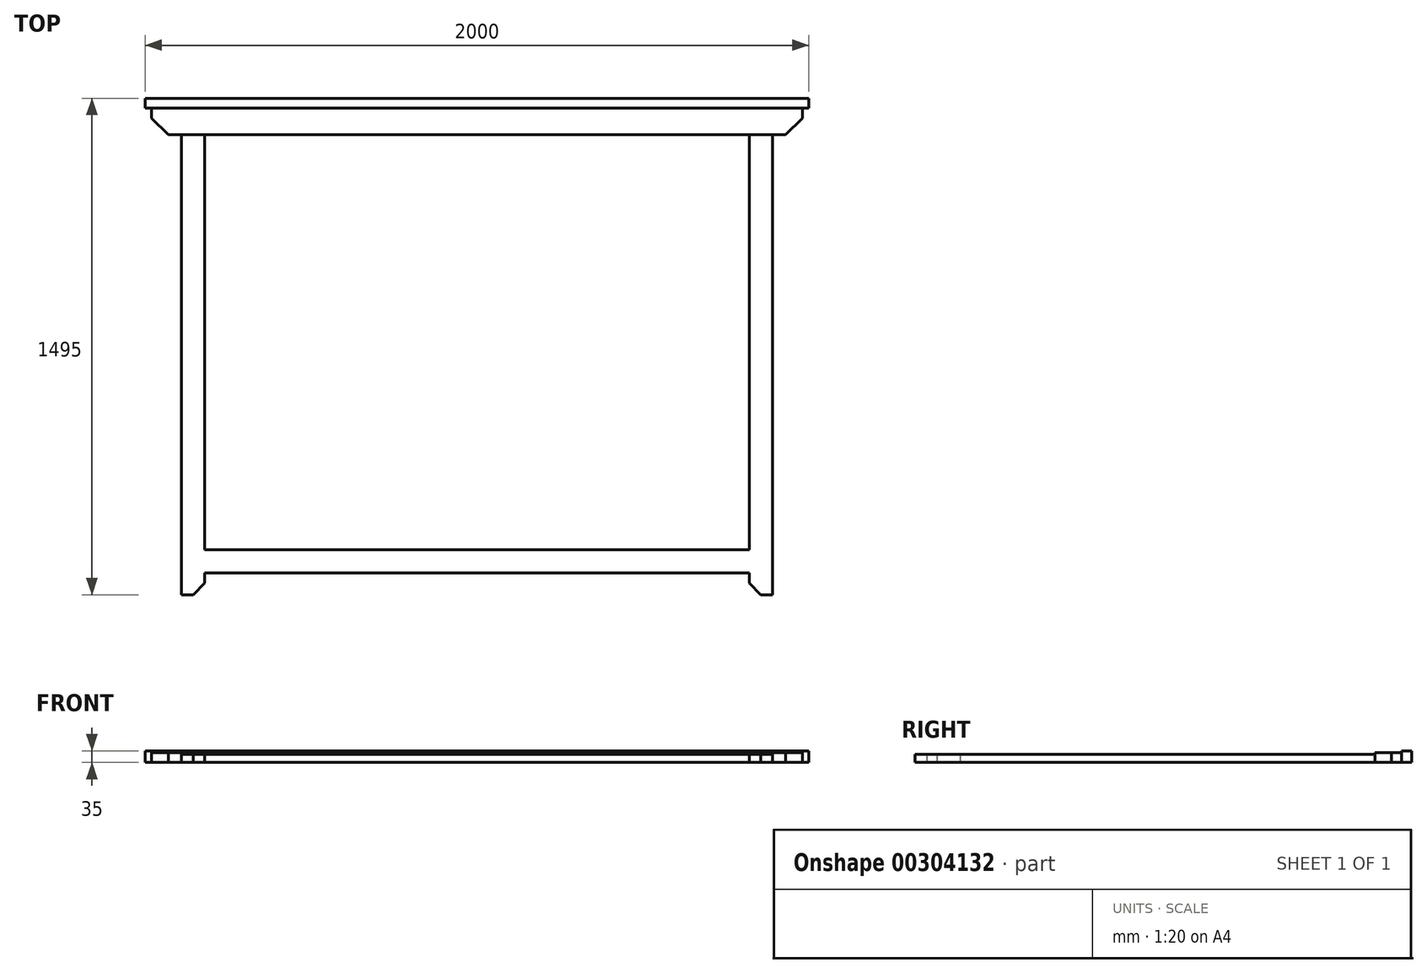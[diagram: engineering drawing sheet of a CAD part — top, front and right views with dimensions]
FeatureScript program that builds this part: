
annotation { "Feature Type Name" : "Feature", "Feature Type Description" : "" }
export const myFeature = defineFeature(function(context is Context, id is Id, definition is map)
    precondition{}
    {
        {
            var Q0;
            Q0=qCreatedBy(makeId("Top.planeOp"),FACE);
            var sketch = newSketch(context, id + "F0", { "sketchPlane" : qUnion([Q0])});
            skLineSegment(sketch, "E0.bottom", {"start": v(-1877.53, -160.44) * mm, "end": v(-237.53, -160.44) * mm});
            skLineSegment(sketch, "E0.top", {"start": v(-1877.53, -1410.44) * mm, "end": v(-237.53, -1410.44) * mm});
            skLineSegment(sketch, "E0.left", {"start": v(-1877.53, -160.44) * mm, "end": v(-1877.53, -1410.44) * mm});
            skLineSegment(sketch, "E0.right", {"start": v(-237.53, -160.44) * mm, "end": v(-237.53, -1410.44) * mm});
            skLineSegment(sketch, "E1", {"start": v(-1877.53, -160.44) * mm, "end": v(-1947.53, -160.44) * mm});
            skLineSegment(sketch, "E2", {"start": v(-2037.53, -110.44) * mm, "end": v(-2037.53, -50.44) * mm});
            skLineSegment(sketch, "E3", {"start": v(-2037.53, -50.44) * mm, "end": v(-77.53, -50.44) * mm});
            skLineSegment(sketch, "E4", {"start": v(-77.53, -50.44) * mm, "end": v(-77.53, -110.44) * mm});
            skLineSegment(sketch, "E5", {"start": v(-167.53, -160.44) * mm, "end": v(-237.53, -160.44) * mm});
            skLineSegment(sketch, "E6", {"start": v(-167.53, -160.44) * mm, "end": v(-167.53, -1545.44) * mm});
            skLineSegment(sketch, "E7", {"start": v(-167.53, -1545.44) * mm, "end": v(-202.53, -1545.44) * mm});
            skLineSegment(sketch, "E8", {"start": v(-237.53, -1480.44) * mm, "end": v(-237.53, -1410.44) * mm});
            skLineSegment(sketch, "E9", {"start": v(-1947.53, -160.44) * mm, "end": v(-1947.53, -1545.44) * mm});
            skLineSegment(sketch, "E10", {"start": v(-1947.53, -1545.44) * mm, "end": v(-1912.53, -1545.44) * mm});
            skLineSegment(sketch, "E11", {"start": v(-1877.53, -1480.44) * mm, "end": v(-1877.53, -1410.44) * mm});
            skLineSegment(sketch, "E12", {"start": v(-1877.53, -1480.44) * mm, "end": v(-237.53, -1480.44) * mm});
            skLineSegment(sketch, "E13", {"start": v(-2037.53, -110.44) * mm, "end": v(-1987.53, -160.44) * mm});
            skLineSegment(sketch, "E14", {"start": v(-1987.53, -160.44) * mm, "end": v(-1947.53, -160.44) * mm});
            skLineSegment(sketch, "E15", {"start": v(-77.53, -110.44) * mm, "end": v(-127.53, -160.44) * mm});
            skLineSegment(sketch, "E16", {"start": v(-127.53, -160.44) * mm, "end": v(-167.53, -160.44) * mm});
            skLineSegment(sketch, "E17", {"start": v(-202.53, -1545.44) * mm, "end": v(-237.53, -1510.44) * mm});
            skLineSegment(sketch, "E18", {"start": v(-237.53, -1510.44) * mm, "end": v(-237.53, -1480.44) * mm});
            skLineSegment(sketch, "E19", {"start": v(-1912.53, -1545.44) * mm, "end": v(-1877.53, -1510.44) * mm});
            skLineSegment(sketch, "E20", {"start": v(-1877.53, -1510.44) * mm, "end": v(-1877.53, -1480.44) * mm});
            skLineSegment(sketch, "E21", {"start": v(-2037.53, -80.44) * mm, "end": v(-77.53, -80.44) * mm});
            skLineSegment(sketch, "E22", {"start": v(-2037.53, -80.44) * mm, "end": v(-2057.53, -80.44) * mm});
            skLineSegment(sketch, "E23", {"start": v(-2057.53, -80.44) * mm, "end": v(-2057.53, -50.44) * mm});
            skLineSegment(sketch, "E24", {"start": v(-2057.53, -50.44) * mm, "end": v(-2037.53, -50.44) * mm});
            skLineSegment(sketch, "E25", {"start": v(-77.53, -50.44) * mm, "end": v(-57.53, -50.44) * mm});
            skLineSegment(sketch, "E26", {"start": v(-57.53, -50.44) * mm, "end": v(-57.53, -80.44) * mm});
            skLineSegment(sketch, "E27", {"start": v(-57.53, -80.44) * mm, "end": v(-77.53, -80.44) * mm});
            skSolve(sketch);
        }
        {
            var Q0;
            Q0=makeQuery(id+"F0.imprint","IMPRINT",FACE,{"disambiguationData":[TD([[makeQuery(id+"F0.imprint","IMPRINT",EDGE,{"derivedFrom":sQuery(id+"F0.wireOp",EDGE,"E0.bottom")}),1.0]])]});
            extrude(context, id + "F1", {"entities" : qUnion([Q0]), "depth" : 30 * mm, "offsetDistance" : 25 * mm});
        }
        {
            var Q0;
            Q0=makeQuery(id+"F0.imprint","IMPRINT",FACE,{"disambiguationData":[TD([[makeQuery(id+"F0.imprint","IMPRINT",EDGE,{"derivedFrom":sQuery(id+"F0.wireOp",EDGE,"E2")}),-1.0]])]});
            var Q1;
            {var subQ0=sQuery(id+"F0.wireOp",EDGE,"E25");Q1=makeQuery(id+"F0.imprint","IMPRINT",FACE,{"disambiguationData":[TD([[makeQuery(id+"F0.imprint","IMPRINT",EDGE,{"derivedFrom":subQ0}),-1.0]])]});}
            var Q2;
            {var subQ2=sQuery(id+"F0.wireOp",EDGE,"E22");Q2=makeQuery(id+"F0.imprint","IMPRINT",FACE,{"disambiguationData":[TD([[makeQuery(id+"F0.imprint","IMPRINT",EDGE,{"derivedFrom":subQ2}),-1.0]])]});}
            extrude(context, id + "F2", {"entities" : qUnion([Q0, Q1, Q2]), "operationType" : NewBodyOperationType.ADD, "depth" : 35 * mm, "offsetDistance" : 25 * mm});
        }
        {
            var Q0;
            Q0=makeQuery(id+"F0.imprint","IMPRINT",FACE,{"disambiguationData":[TD([[makeQuery(id+"F0.imprint","IMPRINT",EDGE,{"derivedFrom":sQuery(id+"F0.wireOp",EDGE,"E0.left")}),-1.0]])]});
            var Q1;
            Q1=makeQuery(id+"F0.imprint","IMPRINT",FACE,{"disambiguationData":[TD([[makeQuery(id+"F0.imprint","IMPRINT",EDGE,{"derivedFrom":sQuery(id+"F0.wireOp",EDGE,"E0.top")}),-1.0]])]});
            var Q2;
            Q2=makeQuery(id+"F0.imprint","IMPRINT",FACE,{"disambiguationData":[TD([[makeQuery(id+"F0.imprint","IMPRINT",EDGE,{"derivedFrom":sQuery(id+"F0.wireOp",EDGE,"E0.right")}),1.0]])]});
            extrude(context, id + "F3", {"entities" : qUnion([Q0, Q1, Q2]), "operationType" : NewBodyOperationType.ADD, "depth" : 25 * mm, "offsetDistance" : 25 * mm});
        }
    });
